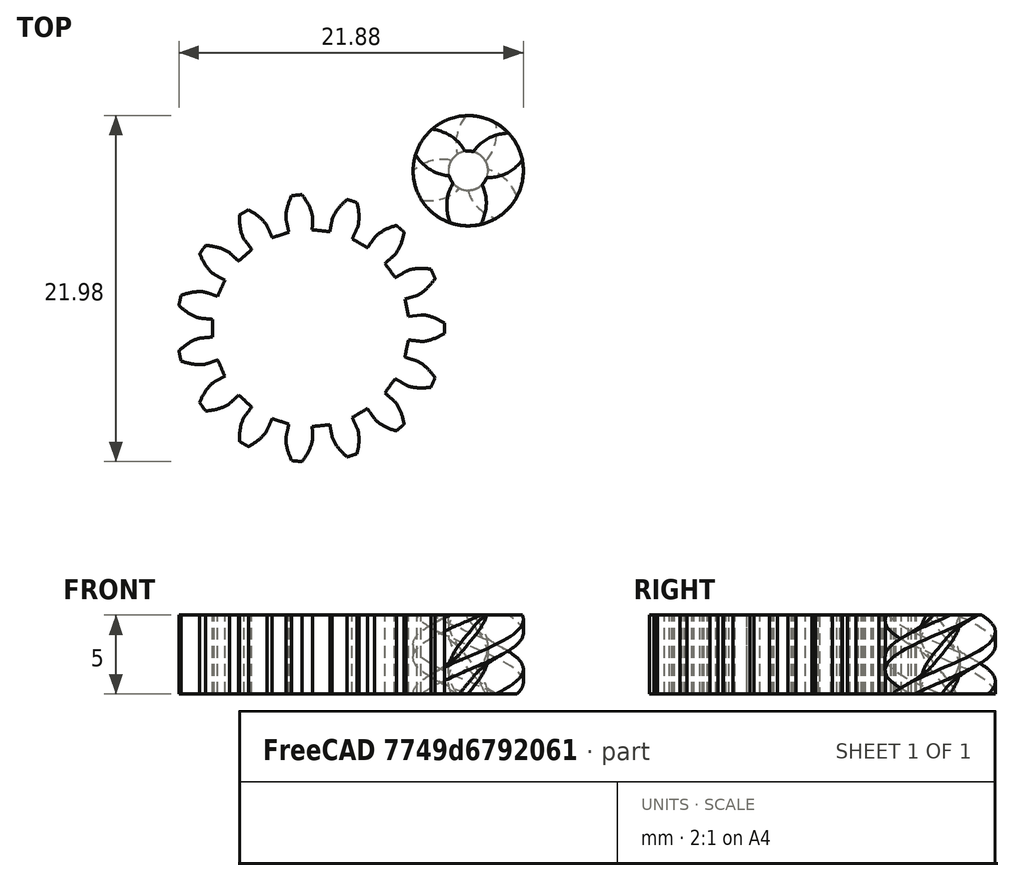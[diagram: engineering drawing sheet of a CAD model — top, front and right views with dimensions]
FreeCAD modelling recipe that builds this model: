
FCSTD DOCUMENT  (FreeCAD 0.20R29603 (Git))
Label: Simple Merge
License: All rights reserved
LicenseURL: http://en.wikipedia.org/wiki/All_rights_reserved
objects: Part::FeaturePython×2, Sketcher::SketchObject×1
note: 3 computed .brp shape members not serialized (recipe doc carries the construction recipe); baked Part::Feature solids carry a one-line shape summary decoded from their .brp

FEATURE [Sketcher::SketchObject] Sketch006
  FullyConstrained = false
  MapMode = 5
  Support = -> [XY_Plane001]
  sketch-geometry (4):
    g0: LineSegment StartX=-7.29585 StartY=-8.06207 StartZ=0 EndX=7.42859 EndY=-8.06207 EndZ=0
    g1: LineSegment StartX=7.42859 StartY=-8.06207 StartZ=0 EndX=7.42859 EndY=8.59056 EndZ=0
    g2: LineSegment StartX=7.42859 StartY=8.59056 StartZ=0 EndX=-7.29585 EndY=8.59056 EndZ=0
    g3: LineSegment StartX=-7.29585 StartY=8.59056 StartZ=0 EndX=-7.29585 EndY=-8.06207 EndZ=0
  constraints (8):
    c: Coincident(g0,g1)
    c: Coincident(g1,g2)
    c: Coincident(g2,g3)
    c: Coincident(g3,g0)
    c: Horizontal(g0)
    c: Horizontal(g2)
    c: Vertical(g1)
    c: Vertical(g3)
FEATURE [Part::FeaturePython] InvoluteGear  # WARN: FeaturePython — macro-defined, semantics opaque (R4)
  AttacherType = Attacher::AttachEngine3D
  Placement = pos=(-20,0,0) rot=(0,0,1;0rad)
  angular_backlash = 0
  backlash = 0
  beta = 0
  clearance = 0.25
  da = 17
  df = 12.5
  double_helix = false
  dw = 15
  head = 0
  head_fillet = 0
  height = 5
  module = 1
  numpoints = 6
  pressure_angle = 20
  properties_from_tool = false
  reversed_backlash = false
  root_fillet = 0
  shift = 0
  simple = false
  teeth = 15
  transverse_pitch = 3.14159
  traverse_module = 1
  undercut = false
  version = 0.0.4
  expr: angular_backlash = backlash / dw * 360 ° / pi
FEATURE [Part::FeaturePython] WormGear  # WARN: FeaturePython — macro-defined, semantics opaque (R4)
  AttacherType = Attacher::AttachEngine3D
  Placement = pos=(-10,10,0) rot=(0,0,1;0rad)
  beta = 30.9638
  clearance = 0.25
  diameter = 5
  head = 0
  height = 5
  module = 1
  pressure_angle = 20
  reverse_pitch = false
  teeth = 3
  version = 0.0.4
